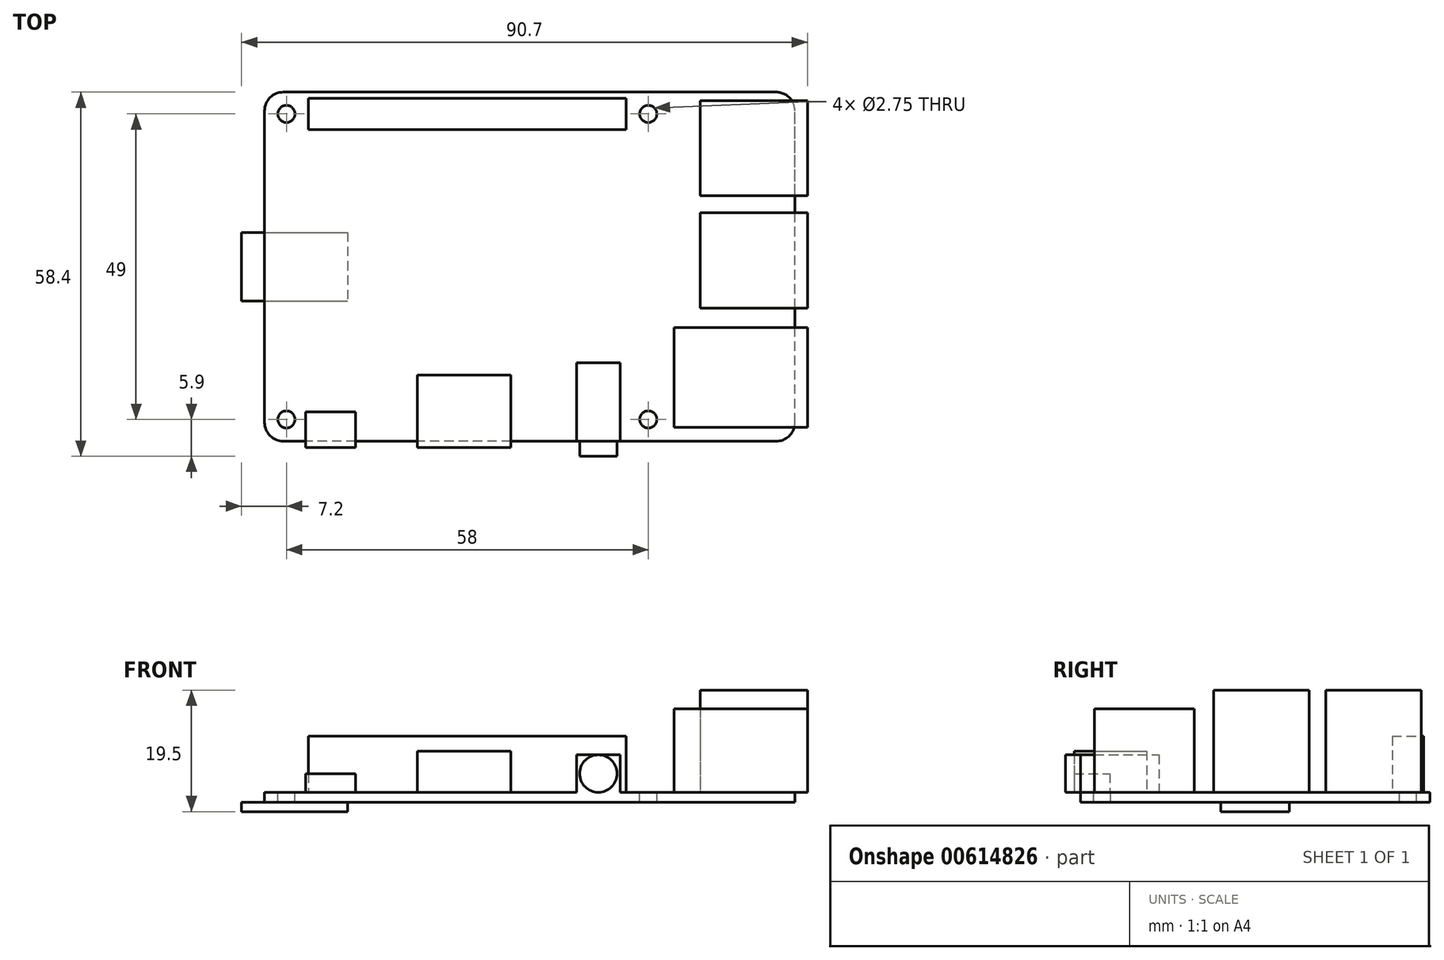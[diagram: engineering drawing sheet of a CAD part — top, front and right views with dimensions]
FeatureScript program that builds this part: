
annotation { "Feature Type Name" : "Feature", "Feature Type Description" : "" }
export const myFeature = defineFeature(function(context is Context, id is Id, definition is map)
    precondition{}
    {
        {
            var Q0;
            Q0=qCreatedBy(makeId("Top.planeOp"),FACE);
            var sketch = newSketch(context, id + "F0", { "sketchPlane" : qUnion([Q0])});
            skLineSegment(sketch, "E0.bottom", {"start": v(42.5, -28) * mm, "end": v(-42.5, -28) * mm});
            skLineSegment(sketch, "E0.top", {"start": v(42.5, 28) * mm, "end": v(-42.5, 28) * mm});
            skLineSegment(sketch, "E0.left", {"start": v(42.5, -28) * mm, "end": v(42.5, 28) * mm});
            skLineSegment(sketch, "E0.right", {"start": v(-42.5, -28) * mm, "end": v(-42.5, 28) * mm});
            skPoint(sketch, "E0.middle", {"position": v(0, 0) * mm});
            skSolve(sketch);
        }
        {
            var Q0;
            Q0 = qSketchRegion(id + "F0", true);
            extrude(context, id + "F1", {"entities" : qUnion([Q0]), "depth" : 1.6 * mm, "offsetDistance" : 25 * mm});
        }
        {
            var Q0;
            Q0=makeQuery(id+"F1.opExtrude","CAP_FACE",FACE,{"disambiguationData":[OSD([sQuery(id+"F0.wireOp",EDGE,"E0.bottom"),sQuery(id+"F0.wireOp",EDGE,"E0.top"),sQuery(id+"F0.wireOp",EDGE,"E0.left"),sQuery(id+"F0.wireOp",EDGE,"E0.right")])],"isStart":false});
            var sketch = newSketch(context, id + "F2", { "sketchPlane" : qUnion([Q0])});
            skLineSegment(sketch, "E1.bottom", {"start": v(44.5, -25.75) * mm, "end": v(23.1, -25.75) * mm});
            skLineSegment(sketch, "E1.top", {"start": v(44.5, -9.75) * mm, "end": v(23.1, -9.75) * mm});
            skLineSegment(sketch, "E1.left", {"start": v(44.5, -25.75) * mm, "end": v(44.5, -9.75) * mm});
            skLineSegment(sketch, "E1.right", {"start": v(23.1, -25.75) * mm, "end": v(23.1, -9.75) * mm});
            skPoint(sketch, "E1.middle", {"position": v(33.8, -17.75) * mm});
            skSolve(sketch);
        }
        {
            var Q0;
            Q0 = qSketchRegion(id + "F2", true);
            extrude(context, id + "F3", {"entities" : qUnion([Q0]), "operationType" : NewBodyOperationType.ADD, "depth" : 13.4 * mm, "offsetDistance" : 25 * mm});
        }
        {
            var Q0;
            Q0=makeQuery(id+"F1.opExtrude","CAP_FACE",FACE,{"disambiguationData":[OSD([sQuery(id+"F0.wireOp",EDGE,"E0.bottom"),sQuery(id+"F0.wireOp",EDGE,"E0.top"),sQuery(id+"F0.wireOp",EDGE,"E0.left"),sQuery(id+"F0.wireOp",EDGE,"E0.right")])],"isStart":false});
            var sketch = newSketch(context, id + "F4", { "sketchPlane" : qUnion([Q0])});
            skLineSegment(sketch, "E2.bottom", {"start": v(44.5, -6.65) * mm, "end": v(27.3, -6.65) * mm});
            skLineSegment(sketch, "E2.top", {"start": v(44.5, 8.65) * mm, "end": v(27.3, 8.65) * mm});
            skLineSegment(sketch, "E2.left", {"start": v(44.5, -6.65) * mm, "end": v(44.5, 8.65) * mm});
            skLineSegment(sketch, "E2.right", {"start": v(27.3, -6.65) * mm, "end": v(27.3, 8.65) * mm});
            skPoint(sketch, "E2.middle", {"position": v(35.9, 1) * mm});
            skLineSegment(sketch, "E3.bottom", {"start": v(44.5, 11.35) * mm, "end": v(27.3, 11.35) * mm});
            skLineSegment(sketch, "E3.top", {"start": v(44.5, 26.65) * mm, "end": v(27.3, 26.65) * mm});
            skLineSegment(sketch, "E3.left", {"start": v(44.5, 11.35) * mm, "end": v(44.5, 26.65) * mm});
            skLineSegment(sketch, "E3.right", {"start": v(27.3, 11.35) * mm, "end": v(27.3, 26.65) * mm});
            skPoint(sketch, "E3.middle", {"position": v(35.9, 19) * mm});
            skSolve(sketch);
        }
        {
            var Q0;
            Q0 = qSketchRegion(id + "F4", true);
            extrude(context, id + "F5", {"entities" : qUnion([Q0]), "operationType" : NewBodyOperationType.ADD, "depth" : 16.4 * mm, "offsetDistance" : 25 * mm});
        }
        {
            var Q0;
            Q0=makeQuery(id+"F1.opExtrude","CAP_FACE",FACE,{"disambiguationData":[OSD([sQuery(id+"F0.wireOp",EDGE,"E0.bottom"),sQuery(id+"F0.wireOp",EDGE,"E0.top"),sQuery(id+"F0.wireOp",EDGE,"E0.left"),sQuery(id+"F0.wireOp",EDGE,"E0.right")])],"isStart":false});
            var sketch = newSketch(context, id + "F6", { "sketchPlane" : qUnion([Q0])});
            skLineSegment(sketch, "E4.bottom", {"start": v(-3, -29) * mm, "end": v(-18, -29) * mm});
            skLineSegment(sketch, "E4.top", {"start": v(-3, -17.4) * mm, "end": v(-18, -17.4) * mm});
            skLineSegment(sketch, "E4.left", {"start": v(-3, -29) * mm, "end": v(-3, -17.4) * mm});
            skLineSegment(sketch, "E4.right", {"start": v(-18, -29) * mm, "end": v(-18, -17.4) * mm});
            skPoint(sketch, "E4.middle", {"position": v(-10.5, -23.2) * mm});
            skSolve(sketch);
        }
        {
            var Q0;
            Q0 = qSketchRegion(id + "F6", true);
            extrude(context, id + "F7", {"entities" : qUnion([Q0]), "operationType" : NewBodyOperationType.ADD, "depth" : 6.6 * mm, "offsetDistance" : 25 * mm});
        }
        {
            var Q0;
            Q0=makeQuery(id+"F1.opExtrude","CAP_FACE",FACE,{"disambiguationData":[OSD([sQuery(id+"F0.wireOp",EDGE,"E0.bottom"),sQuery(id+"F0.wireOp",EDGE,"E0.top"),sQuery(id+"F0.wireOp",EDGE,"E0.left"),sQuery(id+"F0.wireOp",EDGE,"E0.right")])],"isStart":false});
            var sketch = newSketch(context, id + "F8", { "sketchPlane" : qUnion([Q0])});
            skLineSegment(sketch, "E5.bottom", {"start": v(14.5, -30.4) * mm, "end": v(7.5, -30.4) * mm});
            skLineSegment(sketch, "E5.top", {"start": v(14.5, -15.4) * mm, "end": v(7.5, -15.4) * mm});
            skLineSegment(sketch, "E5.left", {"start": v(14.5, -30.4) * mm, "end": v(14.5, -15.4) * mm});
            skLineSegment(sketch, "E5.right", {"start": v(7.5, -30.4) * mm, "end": v(7.5, -15.4) * mm});
            skPoint(sketch, "E5.middle", {"position": v(11, -22.9) * mm});
            skSolve(sketch);
        }
        {
            var Q0;
            Q0 = qSketchRegion(id + "F8", true);
            extrude(context, id + "F9", {"entities" : qUnion([Q0]), "operationType" : NewBodyOperationType.ADD, "depth" : 6 * mm, "offsetDistance" : 25 * mm});
        }
        {
            var Q0;
            Q0=makeQuery(id+"F1.opExtrude","CAP_FACE",FACE,{"disambiguationData":[OSD([sQuery(id+"F0.wireOp",EDGE,"E0.bottom"),sQuery(id+"F0.wireOp",EDGE,"E0.top"),sQuery(id+"F0.wireOp",EDGE,"E0.left"),sQuery(id+"F0.wireOp",EDGE,"E0.right")])],"isStart":false});
            var sketch = newSketch(context, id + "F10", { "sketchPlane" : qUnion([Q0])});
            skLineSegment(sketch, "E6.bottom", {"start": v(-27.9, -29) * mm, "end": v(-35.9, -29) * mm});
            skLineSegment(sketch, "E6.top", {"start": v(-27.9, -23.3) * mm, "end": v(-35.9, -23.3) * mm});
            skLineSegment(sketch, "E6.left", {"start": v(-27.9, -29) * mm, "end": v(-27.9, -23.3) * mm});
            skLineSegment(sketch, "E6.right", {"start": v(-35.9, -29) * mm, "end": v(-35.9, -23.3) * mm});
            skPoint(sketch, "E6.middle", {"position": v(-31.9, -26.15) * mm});
            skSolve(sketch);
        }
        {
            var Q0;
            Q0 = qSketchRegion(id + "F10", true);
            extrude(context, id + "F11", {"entities" : qUnion([Q0]), "operationType" : NewBodyOperationType.ADD, "depth" : 3 * mm, "offsetDistance" : 25 * mm});
        }
        {
            var Q0;
            Q0=makeQuery(id+"F1.opExtrude","CAP_FACE",FACE,{"disambiguationData":[OSD([sQuery(id+"F0.wireOp",EDGE,"E0.bottom"),sQuery(id+"F0.wireOp",EDGE,"E0.top"),sQuery(id+"F0.wireOp",EDGE,"E0.left"),sQuery(id+"F0.wireOp",EDGE,"E0.right")])],"isStart":true});
            var sketch = newSketch(context, id + "F12", { "sketchPlane" : qUnion([Q0])});
            skLineSegment(sketch, "E7.bottom", {"start": v(-46.2, -5.5) * mm, "end": v(-29.2, -5.5) * mm});
            skLineSegment(sketch, "E7.top", {"start": v(-46.2, 5.5) * mm, "end": v(-29.2, 5.5) * mm});
            skLineSegment(sketch, "E7.left", {"start": v(-46.2, -5.5) * mm, "end": v(-46.2, 5.5) * mm});
            skLineSegment(sketch, "E7.right", {"start": v(-29.2, -5.5) * mm, "end": v(-29.2, 5.5) * mm});
            skPoint(sketch, "E7.middle", {"position": v(-37.7, 0) * mm});
            skSolve(sketch);
        }
        {
            var Q0;
            Q0 = qSketchRegion(id + "F12", true);
            extrude(context, id + "F13", {"entities" : qUnion([Q0]), "operationType" : NewBodyOperationType.ADD, "depth" : 1.5 * mm, "offsetDistance" : 25 * mm});
        }
        {
            var Q0;
            Q0=makeQuery(id+"F1.opExtrude","CAP_FACE",FACE,{"disambiguationData":[OSD([sQuery(id+"F0.wireOp",EDGE,"E0.bottom"),sQuery(id+"F0.wireOp",EDGE,"E0.top"),sQuery(id+"F0.wireOp",EDGE,"E0.left"),sQuery(id+"F0.wireOp",EDGE,"E0.right")])],"isStart":false});
            var sketch = newSketch(context, id + "F14", { "sketchPlane" : qUnion([Q0])});
            skCircle(sketch, "E8", {"center": v(-39, -24.5) * mm, "radius": 1.38 * mm});
            skCircle(sketch, "E9", {"center": v(19, -24.5) * mm, "radius": 1.38 * mm});
            skCircle(sketch, "E10.MirrorC", {"center": v(-39, 24.5) * mm, "radius": 1.38 * mm});
            skCircle(sketch, "E11.MirrorC", {"center": v(19, 24.5) * mm, "radius": 1.38 * mm});
            skSolve(sketch);
        }
        {
            var Q0;
            Q0 = qSketchRegion(id + "F14", true);
            extrude(context, id + "F15", {"entities" : qUnion([Q0]), "operationType" : NewBodyOperationType.REMOVE, "endBound" : BoundingType.THROUGH_ALL, "oppositeDirection" : true, "depth" : 25 * mm, "offsetDistance" : 25 * mm});
        }
        {
            var Q0;
            Q0=makeQuery(id+"F1.opExtrude","SWEPT_EDGE",EDGE,{"disambiguationData":[OSD([sQuery(id+"F0.wireOp",EDGE,"E0.bottom"),sQuery(id+"F0.wireOp",EDGE,"E0.right")])]});
            var Q1;
            Q1=makeQuery(id+"F1.opExtrude","SWEPT_EDGE",EDGE,{"disambiguationData":[OSD([sQuery(id+"F0.wireOp",EDGE,"E0.bottom"),sQuery(id+"F0.wireOp",EDGE,"E0.left")])]});
            var Q2;
            Q2=makeQuery(id+"F1.opExtrude","SWEPT_EDGE",EDGE,{"disambiguationData":[OSD([sQuery(id+"F0.wireOp",EDGE,"E0.top"),sQuery(id+"F0.wireOp",EDGE,"E0.left")])]});
            var Q3;
            Q3=makeQuery(id+"F1.opExtrude","SWEPT_EDGE",EDGE,{"disambiguationData":[OSD([sQuery(id+"F0.wireOp",EDGE,"E0.top"),sQuery(id+"F0.wireOp",EDGE,"E0.right")])]});
            fillet(context, id + "F16", {"entities" : qUnion([Q0, Q1, Q2, Q3]), "radius" : 3 * mm, "tangentPropagation" : true, "allowEdgeOverflow" : false});
        }
        {
            var Q0;
            Q0=makeQuery(id+"F1.opExtrude","CAP_FACE",FACE,{"disambiguationData":[OSD([sQuery(id+"F0.wireOp",EDGE,"E0.bottom"),sQuery(id+"F0.wireOp",EDGE,"E0.top"),sQuery(id+"F0.wireOp",EDGE,"E0.left"),sQuery(id+"F0.wireOp",EDGE,"E0.right")])],"isStart":false});
            var sketch = newSketch(context, id + "F17", { "sketchPlane" : qUnion([Q0])});
            skLineSegment(sketch, "E12.bottom", {"start": v(15.45, 21.98) * mm, "end": v(-35.45, 21.98) * mm});
            skLineSegment(sketch, "E12.top", {"start": v(15.45, 26.98) * mm, "end": v(-35.45, 26.98) * mm});
            skLineSegment(sketch, "E12.left", {"start": v(15.45, 21.98) * mm, "end": v(15.45, 26.98) * mm});
            skLineSegment(sketch, "E12.right", {"start": v(-35.45, 21.98) * mm, "end": v(-35.45, 26.98) * mm});
            skPoint(sketch, "E12.middle", {"position": v(-10, 24.48) * mm});
            skSolve(sketch);
        }
        {
            var Q0;
            Q0 = qSketchRegion(id + "F17", true);
            extrude(context, id + "F18", {"entities" : qUnion([Q0]), "operationType" : NewBodyOperationType.ADD, "depth" : 9 * mm, "offsetDistance" : 25 * mm});
        }
        {
            var Q0;
            Q0=makeQuery(id+"F9.opExtrude","SWEPT_FACE",FACE,{"disambiguationData":[OSD([sQuery(id+"F8.wireOp",EDGE,"E5.bottom")])]});
            var sketch = newSketch(context, id + "F19", { "sketchPlane" : qUnion([Q0])});
            skCircle(sketch, "E13", {"center": v(11, 4.6) * mm, "radius": 3 * mm});
            skPoint(sketch, "E13.centerSnap0", {"position": v(11, 7.6) * mm});
            skPoint(sketch, "E13.centerSnap1", {"position": v(7.5, 4.6) * mm});
            skLineSegment(sketch, "E14.bottom", {"start": v(14.5, 1.6) * mm, "end": v(7.5, 1.6) * mm});
            skLineSegment(sketch, "E14.top", {"start": v(14.5, 7.6) * mm, "end": v(7.5, 7.6) * mm});
            skLineSegment(sketch, "E14.left", {"start": v(14.5, 1.6) * mm, "end": v(14.5, 7.6) * mm});
            skLineSegment(sketch, "E14.right", {"start": v(7.5, 1.6) * mm, "end": v(7.5, 7.6) * mm});
            skSolve(sketch);
        }
        {
            var Q0;
            {var subQ5=sQuery(id+"F19.wireOp",EDGE,"E14.left");Q0=makeQuery(id+"F19.imprint","IMPRINT",FACE,{"disambiguationData":[TD([[makeQuery(id+"F19.imprint","IMPRINT",EDGE,{"derivedFrom":subQ5}),-1.0]])]});}
            var Q1;
            {var subQ5=sQuery(id+"F19.wireOp",EDGE,"E14.right");Q1=makeQuery(id+"F19.imprint","IMPRINT",FACE,{"disambiguationData":[TD([[makeQuery(id+"F19.imprint","IMPRINT",EDGE,{"derivedFrom":subQ5}),1.0]])]});}
            extrude(context, id + "F20", {"entities" : qUnion([Q0, Q1]), "operationType" : NewBodyOperationType.REMOVE, "oppositeDirection" : true, "depth" : 2.4 * mm, "offsetDistance" : 25 * mm});
        }
    });
